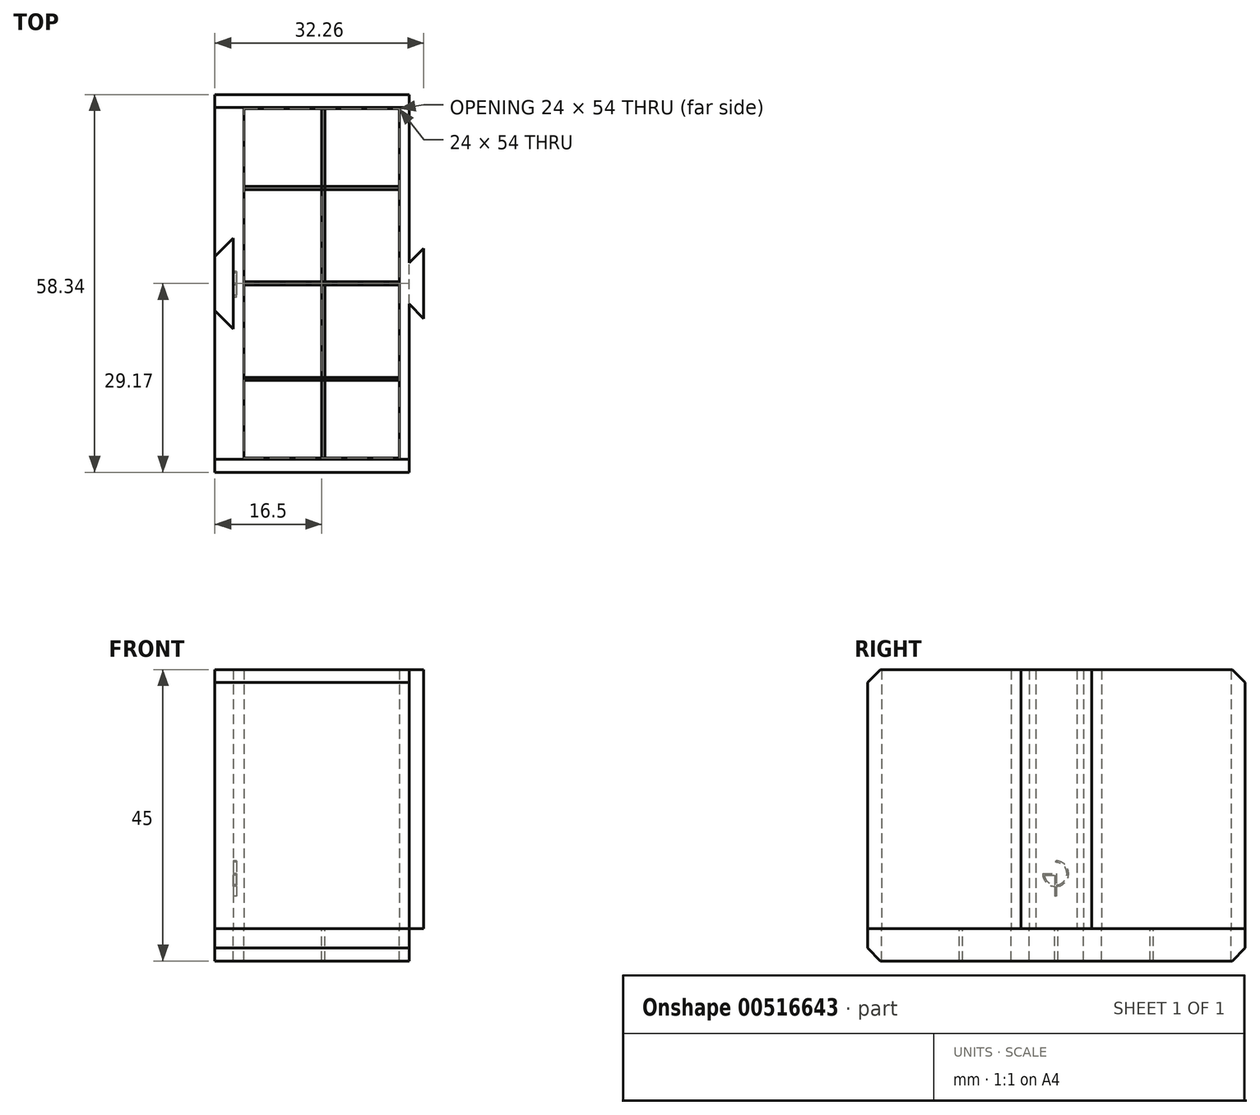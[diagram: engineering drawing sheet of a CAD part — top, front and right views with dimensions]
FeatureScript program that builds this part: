
annotation { "Feature Type Name" : "Feature", "Feature Type Description" : "" }
export const myFeature = defineFeature(function(context is Context, id is Id, definition is map)
    precondition{}
    {
        {
            var Q0;
            Q0=qCreatedBy(makeId("Top.planeOp"),FACE);
            var sketch = newSketch(context, id + "F0", { "sketchPlane" : qUnion([Q0])});
            skLineSegment(sketch, "E0", {"start": v(-15, 4.17) * mm, "end": v(-15, 29.17) * mm});
            skLineSegment(sketch, "E1", {"start": v(-15, 29.17) * mm, "end": v(15, 29.17) * mm});
            skLineSegment(sketch, "E2", {"start": v(15, 29.17) * mm, "end": v(15, 3.17) * mm});
            skLineSegment(sketch, "E3", {"start": v(-15, 4.17) * mm, "end": v(-12.17, 7) * mm});
            skLineSegment(sketch, "E4", {"start": v(-12.17, 7) * mm, "end": v(-12.17, 0) * mm});
            skLineSegment(sketch, "E5", {"start": v(15, 3.17) * mm, "end": v(17.26, 5.43) * mm});
            skLineSegment(sketch, "E6", {"start": v(17.26, 5.43) * mm, "end": v(17.26, -0.57) * mm});
            skLineSegment(sketch, "E7.MirrorCS", {"start": v(-15, -4.17) * mm, "end": v(-12.17, -7) * mm});
            skLineSegment(sketch, "E8.MirrorCS", {"start": v(15, -29.17) * mm, "end": v(15, -3.17) * mm});
            skLineSegment(sketch, "E9.MirrorCS", {"start": v(-12.17, -7) * mm, "end": v(-12.17, 0) * mm});
            skLineSegment(sketch, "E10.MirrorCS", {"start": v(-15, -4.17) * mm, "end": v(-15, -29.17) * mm});
            skLineSegment(sketch, "E11.MirrorCS", {"start": v(17.26, -5.43) * mm, "end": v(17.26, 0.57) * mm});
            skLineSegment(sketch, "E12.MirrorCS", {"start": v(15, -3.17) * mm, "end": v(17.26, -5.43) * mm});
            skLineSegment(sketch, "E13.MirrorCS", {"start": v(-15, -29.17) * mm, "end": v(15, -29.17) * mm});
            skLineSegment(sketch, "E14.bottom", {"start": v(-10.5, 27) * mm, "end": v(13.5, 27) * mm});
            skLineSegment(sketch, "E14.top", {"start": v(-10.5, -27) * mm, "end": v(13.5, -27) * mm});
            skLineSegment(sketch, "E14.left", {"start": v(-10.5, 27) * mm, "end": v(-10.5, -27) * mm});
            skLineSegment(sketch, "E14.right", {"start": v(13.5, 27) * mm, "end": v(13.5, -27) * mm});
            skPoint(sketch, "E14.middle", {"position": v(4, -0.5) * mm});
            skLineSegment(sketch, "E15", {"start": v(-15, 4.17) * mm, "end": v(-15, -4.17) * mm});
            skLineSegment(sketch, "E16", {"start": v(15, -3.17) * mm, "end": v(15, 3.17) * mm});
            skLineSegment(sketch, "E17.bottom", {"start": v(-10.5, 15) * mm, "end": v(13.5, 15) * mm});
            skLineSegment(sketch, "E17.top", {"start": v(-10.5, 14.5) * mm, "end": v(13.5, 14.5) * mm});
            skLineSegment(sketch, "E17.left", {"start": v(-10.5, 15) * mm, "end": v(-10.5, 14.5) * mm});
            skLineSegment(sketch, "E17.right", {"start": v(13.5, 15) * mm, "end": v(13.5, 14.5) * mm});
            skLineSegment(sketch, "E18.bottom", {"start": v(-10.5, -14.5) * mm, "end": v(13.5, -14.5) * mm});
            skLineSegment(sketch, "E18.top", {"start": v(-10.5, -15) * mm, "end": v(13.5, -15) * mm});
            skLineSegment(sketch, "E18.left", {"start": v(-10.5, -14.5) * mm, "end": v(-10.5, -15) * mm});
            skLineSegment(sketch, "E18.right", {"start": v(13.5, -14.5) * mm, "end": v(13.5, -15) * mm});
            skLineSegment(sketch, "E19.bottom", {"start": v(-10.5, 0.25) * mm, "end": v(13.5, 0.25) * mm});
            skLineSegment(sketch, "E19.top", {"start": v(-10.5, -0.25) * mm, "end": v(13.5, -0.25) * mm});
            skLineSegment(sketch, "E19.left", {"start": v(-10.5, 0.25) * mm, "end": v(-10.5, -0.25) * mm});
            skLineSegment(sketch, "E19.right", {"start": v(13.5, 0.25) * mm, "end": v(13.5, -0.25) * mm});
            skLineSegment(sketch, "E20.bottom", {"start": v(1.5, 27) * mm, "end": v(2, 27) * mm});
            skLineSegment(sketch, "E20.top", {"start": v(1.5, -27) * mm, "end": v(2, -27) * mm});
            skLineSegment(sketch, "E20.left", {"start": v(1.5, 27) * mm, "end": v(1.5, -27) * mm});
            skLineSegment(sketch, "E20.right", {"start": v(2, 27) * mm, "end": v(2, -27) * mm});
            skSolve(sketch);
        }
        {
            var Q0;
            Q0=makeQuery(id+"F0.imprint","IMPRINT",FACE,{"disambiguationData":[TD([[makeQuery(id+"F0.imprint","IMPRINT",EDGE,{"derivedFrom":sQuery(id+"F0.wireOp",EDGE,"E5")}),-1.0]])]});
            var Q1;
            Q1=makeQuery(id+"F0.imprint","IMPRINT",FACE,{"disambiguationData":[TD([[makeQuery(id+"F0.imprint","IMPRINT",EDGE,{"derivedFrom":sQuery(id+"F0.wireOp",EDGE,"E0")}),-1.0]])]});
            extrude(context, id + "F1", {"entities" : qUnion([Q0, Q1]), "depth" : 40 * mm, "offsetDistance" : 25 * mm});
        }
        {
            var Q0;
            Q0=makeQuery(id+"F0.imprint","IMPRINT",FACE,{"disambiguationData":[TD([[makeQuery(id+"F0.imprint","IMPRINT",EDGE,{"derivedFrom":sQuery(id+"F0.wireOp",EDGE,"E0")}),-1.0]])]});
            var Q1;
            Q1=makeQuery(id+"F0.imprint","IMPRINT",FACE,{"disambiguationData":[TD([[makeQuery(id+"F0.imprint","IMPRINT",EDGE,{"derivedFrom":sQuery(id+"F0.wireOp",EDGE,"E3")}),-1.0]])]});
            var Q2;
            {var subQ5=sQuery(id+"F0.wireOp",EDGE,"E20.top");Q2=makeQuery(id+"F0.imprint","IMPRINT",FACE,{"disambiguationData":[TD([[makeQuery(id+"F0.imprint","IMPRINT",EDGE,{"derivedFrom":subQ5}),1.0]])]});}
            var Q3;
            {var subQ0=sQuery(id+"F0.wireOp",EDGE,"E14.right");var subQ1=sQuery(id+"F0.wireOp",EDGE,"E14.top");var subQ2=makeQuery(id+"F0.imprint","INTERSECT",VERTEX,{"derivedFrom":[subQ1,subQ0]});Q3=makeQuery(id+"F0.imprint","IMPRINT",FACE,{"disambiguationData":[TD([[makeQuery(id+"F0.imprint","IMPRINT",EDGE,{"disambiguationData":[TD([[subQ2,1.0]])],"derivedFrom":subQ1}),1.0]])]});}
            var Q4;
            {var subQ0=sQuery(id+"F0.wireOp",EDGE,"E14.left");var subQ1=sQuery(id+"F0.wireOp",EDGE,"E14.top");var subQ2=makeQuery(id+"F0.imprint","INTERSECT",VERTEX,{"derivedFrom":[subQ1,subQ0]});Q4=makeQuery(id+"F0.imprint","IMPRINT",FACE,{"disambiguationData":[TD([[makeQuery(id+"F0.imprint","IMPRINT",EDGE,{"disambiguationData":[TD([[subQ2,-1.0]])],"derivedFrom":subQ1}),1.0]])]});}
            var Q5;
            {var subQ0=sQuery(id+"F0.wireOp",EDGE,"E18.left");Q5=makeQuery(id+"F0.imprint","IMPRINT",FACE,{"disambiguationData":[TD([[makeQuery(id+"F0.imprint","IMPRINT",EDGE,{"derivedFrom":subQ0}),1.0]])]});}
            var Q6;
            {var subQ0=sQuery(id+"F0.wireOp",EDGE,"E20.left");var subQ1=sQuery(id+"F0.wireOp",EDGE,"E18.bottom");var subQ2=makeQuery(id+"F0.imprint","INTERSECT",VERTEX,{"derivedFrom":[subQ1,subQ0]});Q6=makeQuery(id+"F0.imprint","IMPRINT",FACE,{"disambiguationData":[TD([[makeQuery(id+"F0.imprint","IMPRINT",EDGE,{"disambiguationData":[TD([[subQ2,-1.0]])],"derivedFrom":subQ1}),-1.0]])]});}
            var Q7;
            {var subQ0=sQuery(id+"F0.wireOp",EDGE,"E20.left");var subQ1=sQuery(id+"F0.wireOp",EDGE,"E18.bottom");var subQ2=makeQuery(id+"F0.imprint","INTERSECT",VERTEX,{"derivedFrom":[subQ1,subQ0]});Q7=makeQuery(id+"F0.imprint","IMPRINT",FACE,{"disambiguationData":[TD([[makeQuery(id+"F0.imprint","IMPRINT",EDGE,{"disambiguationData":[TD([[subQ2,-1.0]])],"derivedFrom":subQ1}),1.0]])]});}
            var Q8;
            {var subQ0=sQuery(id+"F0.wireOp",EDGE,"E18.bottom");var subQ5=sQuery(id+"F0.wireOp",EDGE,"E20.left");var subQ6=makeQuery(id+"F0.imprint","INTERSECT",VERTEX,{"derivedFrom":[subQ0,subQ5]});Q8=makeQuery(id+"F0.imprint","IMPRINT",FACE,{"disambiguationData":[TD([[makeQuery(id+"F0.imprint","IMPRINT",EDGE,{"disambiguationData":[TD([[subQ6,1.0]])],"derivedFrom":subQ5}),-1.0]])]});}
            var Q9;
            {var subQ0=sQuery(id+"F0.wireOp",EDGE,"E18.bottom");var subQ5=sQuery(id+"F0.wireOp",EDGE,"E20.right");var subQ7=makeQuery(id+"F0.imprint","INTERSECT",VERTEX,{"derivedFrom":[subQ0,subQ5]});Q9=makeQuery(id+"F0.imprint","IMPRINT",FACE,{"disambiguationData":[TD([[makeQuery(id+"F0.imprint","IMPRINT",EDGE,{"disambiguationData":[TD([[subQ7,1.0]])],"derivedFrom":subQ5}),1.0]])]});}
            var Q10;
            {var subQ0=sQuery(id+"F0.wireOp",EDGE,"E17.top");var subQ5=sQuery(id+"F0.wireOp",EDGE,"E20.right");var subQ6=makeQuery(id+"F0.imprint","INTERSECT",VERTEX,{"derivedFrom":[subQ0,subQ5]});Q10=makeQuery(id+"F0.imprint","IMPRINT",FACE,{"disambiguationData":[TD([[makeQuery(id+"F0.imprint","IMPRINT",EDGE,{"disambiguationData":[TD([[subQ6,-1.0]])],"derivedFrom":subQ5}),1.0]])]});}
            var Q11;
            {var subQ0=sQuery(id+"F0.wireOp",EDGE,"E17.top");var subQ5=sQuery(id+"F0.wireOp",EDGE,"E20.left");var subQ7=makeQuery(id+"F0.imprint","INTERSECT",VERTEX,{"derivedFrom":[subQ0,subQ5]});Q11=makeQuery(id+"F0.imprint","IMPRINT",FACE,{"disambiguationData":[TD([[makeQuery(id+"F0.imprint","IMPRINT",EDGE,{"disambiguationData":[TD([[subQ7,-1.0]])],"derivedFrom":subQ5}),-1.0]])]});}
            var Q12;
            {var subQ0=sQuery(id+"F0.wireOp",EDGE,"E20.left");var subQ1=sQuery(id+"F0.wireOp",EDGE,"E19.bottom");var subQ2=makeQuery(id+"F0.imprint","INTERSECT",VERTEX,{"derivedFrom":[subQ1,subQ0]});Q12=makeQuery(id+"F0.imprint","IMPRINT",FACE,{"disambiguationData":[TD([[makeQuery(id+"F0.imprint","IMPRINT",EDGE,{"disambiguationData":[TD([[subQ2,-1.0]])],"derivedFrom":subQ1}),-1.0]])]});}
            var Q13;
            {var subQ0=sQuery(id+"F0.wireOp",EDGE,"E20.left");var subQ1=sQuery(id+"F0.wireOp",EDGE,"E17.top");var subQ2=makeQuery(id+"F0.imprint","INTERSECT",VERTEX,{"derivedFrom":[subQ1,subQ0]});Q13=makeQuery(id+"F0.imprint","IMPRINT",FACE,{"disambiguationData":[TD([[makeQuery(id+"F0.imprint","IMPRINT",EDGE,{"disambiguationData":[TD([[subQ2,-1.0]])],"derivedFrom":subQ1}),-1.0]])]});}
            var Q14;
            {var subQ0=sQuery(id+"F0.wireOp",EDGE,"E17.right");Q14=makeQuery(id+"F0.imprint","IMPRINT",FACE,{"disambiguationData":[TD([[makeQuery(id+"F0.imprint","IMPRINT",EDGE,{"derivedFrom":subQ0}),-1.0]])]});}
            var Q15;
            {var subQ0=sQuery(id+"F0.wireOp",EDGE,"E20.left");var subQ1=sQuery(id+"F0.wireOp",EDGE,"E17.bottom");var subQ2=makeQuery(id+"F0.imprint","INTERSECT",VERTEX,{"derivedFrom":[subQ1,subQ0]});Q15=makeQuery(id+"F0.imprint","IMPRINT",FACE,{"disambiguationData":[TD([[makeQuery(id+"F0.imprint","IMPRINT",EDGE,{"disambiguationData":[TD([[subQ2,-1.0]])],"derivedFrom":subQ1}),-1.0]])]});}
            var Q16;
            {var subQ0=sQuery(id+"F0.wireOp",EDGE,"E17.left");Q16=makeQuery(id+"F0.imprint","IMPRINT",FACE,{"disambiguationData":[TD([[makeQuery(id+"F0.imprint","IMPRINT",EDGE,{"derivedFrom":subQ0}),1.0]])]});}
            var Q17;
            {var subQ0=sQuery(id+"F0.wireOp",EDGE,"E14.left");var subQ1=sQuery(id+"F0.wireOp",EDGE,"E14.bottom");var subQ2=makeQuery(id+"F0.imprint","INTERSECT",VERTEX,{"derivedFrom":[subQ1,subQ0]});Q17=makeQuery(id+"F0.imprint","IMPRINT",FACE,{"disambiguationData":[TD([[makeQuery(id+"F0.imprint","IMPRINT",EDGE,{"disambiguationData":[TD([[subQ2,-1.0]])],"derivedFrom":subQ1}),-1.0]])]});}
            var Q18;
            {var subQ0=sQuery(id+"F0.wireOp",EDGE,"E14.right");var subQ1=sQuery(id+"F0.wireOp",EDGE,"E14.bottom");var subQ2=makeQuery(id+"F0.imprint","INTERSECT",VERTEX,{"derivedFrom":[subQ1,subQ0]});Q18=makeQuery(id+"F0.imprint","IMPRINT",FACE,{"disambiguationData":[TD([[makeQuery(id+"F0.imprint","IMPRINT",EDGE,{"disambiguationData":[TD([[subQ2,1.0]])],"derivedFrom":subQ1}),-1.0]])]});}
            var Q19;
            {var subQ5=sQuery(id+"F0.wireOp",EDGE,"E20.bottom");Q19=makeQuery(id+"F0.imprint","IMPRINT",FACE,{"disambiguationData":[TD([[makeQuery(id+"F0.imprint","IMPRINT",EDGE,{"derivedFrom":subQ5}),-1.0]])]});}
            var Q20;
            {var subQ0=sQuery(id+"F0.wireOp",EDGE,"E19.left");Q20=makeQuery(id+"F0.imprint","IMPRINT",FACE,{"disambiguationData":[TD([[makeQuery(id+"F0.imprint","IMPRINT",EDGE,{"derivedFrom":subQ0}),1.0]])]});}
            var Q21;
            {var subQ0=sQuery(id+"F0.wireOp",EDGE,"E19.right");Q21=makeQuery(id+"F0.imprint","IMPRINT",FACE,{"disambiguationData":[TD([[makeQuery(id+"F0.imprint","IMPRINT",EDGE,{"derivedFrom":subQ0}),-1.0]])]});}
            var Q22;
            {var subQ0=sQuery(id+"F0.wireOp",EDGE,"E18.right");Q22=makeQuery(id+"F0.imprint","IMPRINT",FACE,{"disambiguationData":[TD([[makeQuery(id+"F0.imprint","IMPRINT",EDGE,{"derivedFrom":subQ0}),-1.0]])]});}
            extrude(context, id + "F2", {"entities" : qUnion([Q0, Q1, Q2, Q3, Q4, Q5, Q6, Q7, Q8, Q9, Q10, Q11, Q12, Q13, Q14, Q15, Q16, Q17, Q18, Q19, Q20, Q21, Q22]), "operationType" : NewBodyOperationType.ADD, "oppositeDirection" : true, "depth" : 5 * mm, "offsetDistance" : 25 * mm});
        }
        {
            var Q0;
            Q0=makeQuery(id+"F2.opExtrude","CAP_EDGE",EDGE,{"disambiguationData":[OSD([sQuery(id+"F0.wireOp",EDGE,"E13.MirrorCS")])],"isStart":false});
            var Q1;
            Q1=makeQuery(id+"F2.opExtrude","CAP_EDGE",EDGE,{"disambiguationData":[OSD([sQuery(id+"F0.wireOp",EDGE,"E1")])],"isStart":false});
            var Q2;
            Q2=makeQuery(id+"F1.opExtrude","CAP_EDGE",EDGE,{"disambiguationData":[OSD([sQuery(id+"F0.wireOp",EDGE,"E13.MirrorCS")])],"isStart":false});
            var Q3;
            Q3=makeQuery(id+"F1.opExtrude","CAP_EDGE",EDGE,{"disambiguationData":[OSD([sQuery(id+"F0.wireOp",EDGE,"E1")])],"isStart":false});
            chamfer(context, id + "F3", {"entities" : qUnion([Q0, Q1, Q2, Q3]), "width" : 2 * mm, "tangentPropagation" : true});
        }
        {
            var Q0;
            Q0=makeQuery(id+"F1.opExtrude","SWEPT_FACE",FACE,{"disambiguationData":[OSD([sQuery(id+"F0.wireOp",EDGE,"E4"),sQuery(id+"F0.wireOp",EDGE,"E9.MirrorCS")])]});
            var sketch = newSketch(context, id + "F4", { "sketchPlane" : qUnion([Q0])});
            skLineSegment(sketch, "E21.bottom", {"start": v(0.12, 10.5) * mm, "end": v(2.12, 10.5) * mm, "construction": true});
            skLineSegment(sketch, "E21.top", {"start": v(0.12, 8.5) * mm, "end": v(2.12, 8.5) * mm, "construction": true});
            skLineSegment(sketch, "E21.left", {"start": v(0.12, 10.5) * mm, "end": v(0.12, 8.5) * mm, "construction": true});
            skLineSegment(sketch, "E21.right", {"start": v(2.12, 10.5) * mm, "end": v(2.12, 8.5) * mm, "construction": true});
            skArc(sketch, "E22", {"start": v(0.12, 10.5) * mm, "mid": v(-1.3, 7.09) * mm, "end": v(2.12, 8.5) * mm});
            skLineSegment(sketch, "E23", {"start": v(0.12, 10.5) * mm, "end": v(0.12, 10.25) * mm});
            skLineSegment(sketch, "E24", {"start": v(2.12, 8.5) * mm, "end": v(1.87, 8.5) * mm});
            skArc(sketch, "E25", {"start": v(0.12, 10.25) * mm, "mid": v(-1.12, 7.26) * mm, "end": v(1.87, 8.5) * mm});
            skLineSegment(sketch, "E26", {"start": v(1.87, 8.5) * mm, "end": v(0, 8.5) * mm});
            skLineSegment(sketch, "E27", {"start": v(0, 8.5) * mm, "end": v(0, 5) * mm});
            skLineSegment(sketch, "E28", {"start": v(0, 5) * mm, "end": v(0.25, 5) * mm});
            skLineSegment(sketch, "E29", {"start": v(1.85, 8.25) * mm, "end": v(0.25, 8.25) * mm});
            skLineSegment(sketch, "E30", {"start": v(0.25, 8.25) * mm, "end": v(0.25, 5) * mm});
            skSolve(sketch);
        }
        {
            var Q0;
            {var subQ0=sQuery(id+"F4.wireOp",EDGE,"E23");Q0=makeQuery(id+"F4.imprint","IMPRINT",FACE,{"disambiguationData":[TD([[makeQuery(id+"F4.imprint","IMPRINT",EDGE,{"derivedFrom":subQ0}),-1.0]])]});}
            var Q1;
            {var subQ1=sQuery(id+"F4.wireOp",EDGE,"E26");Q1=makeQuery(id+"F4.imprint","IMPRINT",FACE,{"disambiguationData":[TD([[makeQuery(id+"F4.imprint","IMPRINT",EDGE,{"derivedFrom":subQ1}),1.0]])]});}
            var Q2;
            {var subQ1=sQuery(id+"F4.wireOp",EDGE,"E24");Q2=makeQuery(id+"F4.imprint","IMPRINT",FACE,{"disambiguationData":[TD([[makeQuery(id+"F4.imprint","IMPRINT",EDGE,{"derivedFrom":subQ1}),1.0]])]});}
            var Q3;
            {var subQ0=sQuery(id+"F4.wireOp",EDGE,"E27");var subQ1=sQuery(id+"F4.wireOp",EDGE,"E22");var subQ2=makeQuery(id+"F4.imprint","INTERSECT",VERTEX,{"derivedFrom":[subQ1,subQ0]});Q3=makeQuery(id+"F4.imprint","IMPRINT",FACE,{"disambiguationData":[TD([[makeQuery(id+"F4.imprint","IMPRINT",EDGE,{"disambiguationData":[TD([[subQ2,-1.0]])],"derivedFrom":subQ1}),1.0]])]});}
            var Q4;
            {var subQ5=sQuery(id+"F4.wireOp",EDGE,"E28");Q4=makeQuery(id+"F4.imprint","IMPRINT",FACE,{"disambiguationData":[TD([[makeQuery(id+"F4.imprint","IMPRINT",EDGE,{"derivedFrom":subQ5}),1.0]])]});}
            extrude(context, id + "F5", {"entities" : qUnion([Q0, Q1, Q2, Q3, Q4]), "operationType" : NewBodyOperationType.REMOVE, "oppositeDirection" : true, "depth" : .5 * mm, "offsetDistance" : 25 * mm});
        }
    });
